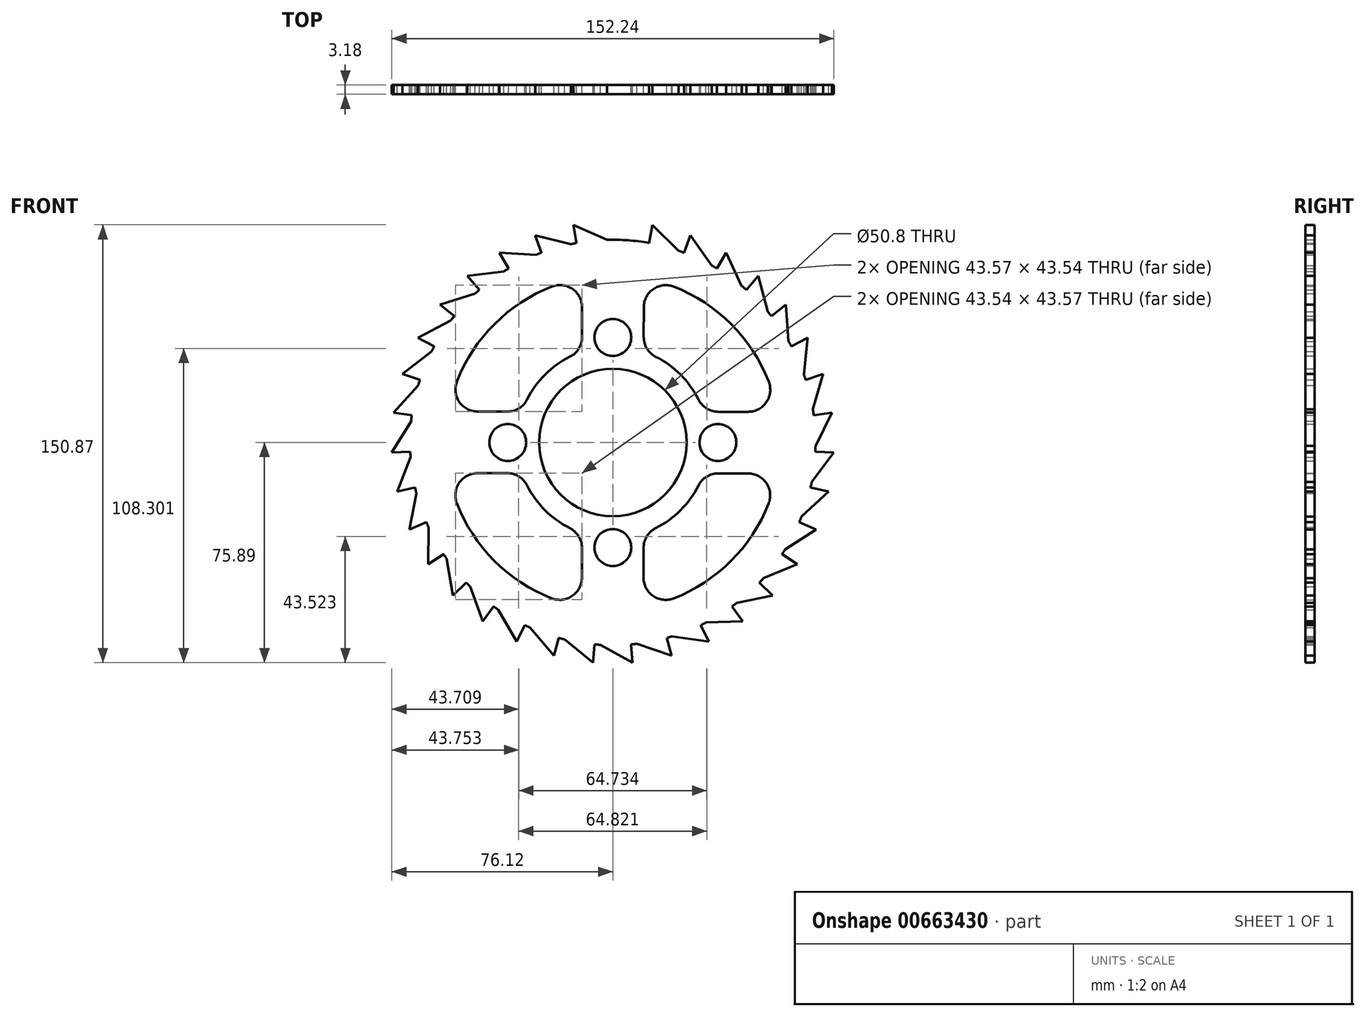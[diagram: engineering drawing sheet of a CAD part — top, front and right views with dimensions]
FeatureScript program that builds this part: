
annotation { "Feature Type Name" : "Feature", "Feature Type Description" : "" }
export const myFeature = defineFeature(function(context is Context, id is Id, definition is map)
    precondition{}
    {
        {
            var Q0;
            Q0=qCreatedBy(makeId("Front.planeOp"),FACE);
            var sketch = newSketch(context, id + "F0", { "sketchPlane" : qUnion([Q0])});
            skCircle(sketch, "E0", {"center": v(0, 0) * mm, "radius": 25.4 * mm});
            skCircle(sketch, "E1", {"center": v(0, 0) * mm, "radius": 69.85 * mm});
            skCircle(sketch, "E2", {"center": v(0, 0) * mm, "radius": 76.2 * mm, "construction": true});
            skLineSegment(sketch, "E3", {"start": v(0, 69.85) * mm, "end": v(0, 76.2) * mm});
            skLineSegment(sketch, "E4", {"start": v(0, 76.2) * mm, "end": v(10.5, 69.06) * mm});
            skLineSegment(sketch, "E5.1.0", {"start": v(13.6, 74.98) * mm, "end": v(22.66, 66.07) * mm});
            skLineSegment(sketch, "E5.1.1", {"start": v(12.47, 68.73) * mm, "end": v(13.6, 74.98) * mm});
            skCircle(sketch, "E5.1.2", {"center": v(0, 0) * mm, "radius": 69.85 * mm, "construction": true});
            skLineSegment(sketch, "E5.2.0", {"start": v(26.77, 71.34) * mm, "end": v(34.1, 60.96) * mm});
            skLineSegment(sketch, "E5.2.1", {"start": v(24.54, 65.4) * mm, "end": v(26.77, 71.34) * mm});
            skCircle(sketch, "E5.2.2", {"center": v(0, 0) * mm, "radius": 69.85 * mm, "construction": true});
            skLineSegment(sketch, "E5.3.0", {"start": v(39.08, 65.41) * mm, "end": v(44.43, 53.9) * mm});
            skLineSegment(sketch, "E5.3.1", {"start": v(35.83, 59.96) * mm, "end": v(39.08, 65.41) * mm});
            skCircle(sketch, "E5.3.2", {"center": v(0, 0) * mm, "radius": 69.85 * mm, "construction": true});
            skLineSegment(sketch, "E5.4.0", {"start": v(50.13, 57.38) * mm, "end": v(53.34, 45.1) * mm});
            skLineSegment(sketch, "E5.4.1", {"start": v(45.96, 52.6) * mm, "end": v(50.13, 57.38) * mm});
            skCircle(sketch, "E5.4.2", {"center": v(0, 0) * mm, "radius": 69.85 * mm, "construction": true});
            skLineSegment(sketch, "E5.5.0", {"start": v(59.58, 47.5) * mm, "end": v(60.54, 34.85) * mm});
            skLineSegment(sketch, "E5.5.1", {"start": v(54.61, 43.55) * mm, "end": v(59.58, 47.5) * mm});
            skCircle(sketch, "E5.5.2", {"center": v(0, 0) * mm, "radius": 69.85 * mm, "construction": true});
            skLineSegment(sketch, "E5.6.0", {"start": v(67.1, 36.1) * mm, "end": v(65.79, 23.48) * mm});
            skLineSegment(sketch, "E5.6.1", {"start": v(61.5, 33.1) * mm, "end": v(67.1, 36.1) * mm});
            skCircle(sketch, "E5.6.2", {"center": v(0, 0) * mm, "radius": 69.85 * mm, "construction": true});
            skLineSegment(sketch, "E5.7.0", {"start": v(72.47, 23.55) * mm, "end": v(68.92, 11.35) * mm});
            skLineSegment(sketch, "E5.7.1", {"start": v(66.43, 21.58) * mm, "end": v(72.47, 23.55) * mm});
            skCircle(sketch, "E5.7.2", {"center": v(0, 0) * mm, "radius": 69.85 * mm, "construction": true});
            skLineSegment(sketch, "E5.8.0", {"start": v(75.51, 10.23) * mm, "end": v(69.84, -1.14) * mm});
            skLineSegment(sketch, "E5.8.1", {"start": v(69.22, 9.38) * mm, "end": v(75.51, 10.23) * mm});
            skCircle(sketch, "E5.8.2", {"center": v(0, 0) * mm, "radius": 69.85 * mm, "construction": true});
            skLineSegment(sketch, "E5.9.0", {"start": v(76.12, -3.42) * mm, "end": v(68.52, -13.59) * mm});
            skLineSegment(sketch, "E5.9.1", {"start": v(69.78, -3.13) * mm, "end": v(76.12, -3.42) * mm});
            skCircle(sketch, "E5.9.2", {"center": v(0, 0) * mm, "radius": 69.85 * mm, "construction": true});
            skLineSegment(sketch, "E5.10.0", {"start": v(74.29, -16.96) * mm, "end": v(64.99, -25.6) * mm});
            skLineSegment(sketch, "E5.10.1", {"start": v(68.1, -15.54) * mm, "end": v(74.29, -16.96) * mm});
            skCircle(sketch, "E5.10.2", {"center": v(0, 0) * mm, "radius": 69.85 * mm, "construction": true});
            skLineSegment(sketch, "E5.11.0", {"start": v(70.07, -29.95) * mm, "end": v(59.37, -36.8) * mm});
            skLineSegment(sketch, "E5.11.1", {"start": v(64.23, -27.45) * mm, "end": v(70.07, -29.95) * mm});
            skCircle(sketch, "E5.11.2", {"center": v(0, 0) * mm, "radius": 69.85 * mm, "construction": true});
            skLineSegment(sketch, "E5.12.0", {"start": v(63.6, -41.98) * mm, "end": v(51.85, -46.8) * mm});
            skLineSegment(sketch, "E5.12.1", {"start": v(58.3, -38.48) * mm, "end": v(63.6, -41.98) * mm});
            skCircle(sketch, "E5.12.2", {"center": v(0, 0) * mm, "radius": 69.85 * mm, "construction": true});
            skLineSegment(sketch, "E5.13.0", {"start": v(55.08, -52.66) * mm, "end": v(42.66, -55.31) * mm});
            skLineSegment(sketch, "E5.13.1", {"start": v(50.49, -48.27) * mm, "end": v(55.08, -52.66) * mm});
            skCircle(sketch, "E5.13.2", {"center": v(0, 0) * mm, "radius": 69.85 * mm, "construction": true});
            skLineSegment(sketch, "E5.14.0", {"start": v(44.79, -61.65) * mm, "end": v(32.1, -62.04) * mm});
            skLineSegment(sketch, "E5.14.1", {"start": v(41.06, -56.5) * mm, "end": v(44.79, -61.65) * mm});
            skCircle(sketch, "E5.14.2", {"center": v(0, 0) * mm, "radius": 69.85 * mm, "construction": true});
            skLineSegment(sketch, "E5.15.0", {"start": v(33.06, -68.65) * mm, "end": v(20.5, -66.77) * mm});
            skLineSegment(sketch, "E5.15.1", {"start": v(30.3, -62.93) * mm, "end": v(33.06, -68.65) * mm});
            skCircle(sketch, "E5.15.2", {"center": v(0, 0) * mm, "radius": 69.85 * mm, "construction": true});
            skLineSegment(sketch, "E5.16.0", {"start": v(20.27, -73.45) * mm, "end": v(8.25, -69.36) * mm});
            skLineSegment(sketch, "E5.16.1", {"start": v(18.58, -67.33) * mm, "end": v(20.27, -73.45) * mm});
            skCircle(sketch, "E5.16.2", {"center": v(0, 0) * mm, "radius": 69.85 * mm, "construction": true});
            skLineSegment(sketch, "E5.17.0", {"start": v(6.83, -75.9) * mm, "end": v(-4.27, -69.72) * mm});
            skLineSegment(sketch, "E5.17.1", {"start": v(6.26, -69.57) * mm, "end": v(6.83, -75.9) * mm});
            skCircle(sketch, "E5.17.2", {"center": v(0, 0) * mm, "radius": 69.85 * mm, "construction": true});
            skLineSegment(sketch, "E5.18.0", {"start": v(-6.83, -75.9) * mm, "end": v(-16.65, -67.84) * mm});
            skLineSegment(sketch, "E5.18.1", {"start": v(-6.26, -69.57) * mm, "end": v(-6.83, -75.9) * mm});
            skCircle(sketch, "E5.18.2", {"center": v(0, 0) * mm, "radius": 69.85 * mm, "construction": true});
            skLineSegment(sketch, "E5.19.0", {"start": v(-20.27, -73.45) * mm, "end": v(-28.5, -63.77) * mm});
            skLineSegment(sketch, "E5.19.1", {"start": v(-18.58, -67.33) * mm, "end": v(-20.27, -73.45) * mm});
            skCircle(sketch, "E5.19.2", {"center": v(0, 0) * mm, "radius": 69.85 * mm, "construction": true});
            skLineSegment(sketch, "E5.20.0", {"start": v(-33.06, -68.65) * mm, "end": v(-39.42, -57.66) * mm});
            skLineSegment(sketch, "E5.20.1", {"start": v(-30.3, -62.93) * mm, "end": v(-33.06, -68.65) * mm});
            skCircle(sketch, "E5.20.2", {"center": v(0, 0) * mm, "radius": 69.85 * mm, "construction": true});
            skLineSegment(sketch, "E5.21.0", {"start": v(-44.79, -61.65) * mm, "end": v(-49.09, -49.7) * mm});
            skLineSegment(sketch, "E5.21.1", {"start": v(-41.06, -56.5) * mm, "end": v(-44.79, -61.65) * mm});
            skCircle(sketch, "E5.21.2", {"center": v(0, 0) * mm, "radius": 69.85 * mm, "construction": true});
            skLineSegment(sketch, "E5.22.0", {"start": v(-55.08, -52.66) * mm, "end": v(-57.17, -40.13) * mm});
            skLineSegment(sketch, "E5.22.1", {"start": v(-50.49, -48.27) * mm, "end": v(-55.08, -52.66) * mm});
            skCircle(sketch, "E5.22.2", {"center": v(0, 0) * mm, "radius": 69.85 * mm, "construction": true});
            skLineSegment(sketch, "E5.23.0", {"start": v(-63.6, -41.98) * mm, "end": v(-63.42, -29.28) * mm});
            skLineSegment(sketch, "E5.23.1", {"start": v(-58.3, -38.48) * mm, "end": v(-63.6, -41.98) * mm});
            skCircle(sketch, "E5.23.2", {"center": v(0, 0) * mm, "radius": 69.85 * mm, "construction": true});
            skLineSegment(sketch, "E5.24.0", {"start": v(-70.07, -29.95) * mm, "end": v(-67.63, -17.49) * mm});
            skLineSegment(sketch, "E5.24.1", {"start": v(-64.23, -27.45) * mm, "end": v(-70.07, -29.95) * mm});
            skCircle(sketch, "E5.24.2", {"center": v(0, 0) * mm, "radius": 69.85 * mm, "construction": true});
            skLineSegment(sketch, "E5.25.0", {"start": v(-74.29, -16.96) * mm, "end": v(-69.66, -5.13) * mm});
            skLineSegment(sketch, "E5.25.1", {"start": v(-68.1, -15.54) * mm, "end": v(-74.29, -16.96) * mm});
            skCircle(sketch, "E5.25.2", {"center": v(0, 0) * mm, "radius": 69.85 * mm, "construction": true});
            skLineSegment(sketch, "E5.26.0", {"start": v(-76.12, -3.42) * mm, "end": v(-69.46, 7.4) * mm});
            skLineSegment(sketch, "E5.26.1", {"start": v(-69.78, -3.13) * mm, "end": v(-76.12, -3.42) * mm});
            skCircle(sketch, "E5.26.2", {"center": v(0, 0) * mm, "radius": 69.85 * mm, "construction": true});
            skLineSegment(sketch, "E5.27.0", {"start": v(-75.51, 10.23) * mm, "end": v(-67.02, 19.67) * mm});
            skLineSegment(sketch, "E5.27.1", {"start": v(-69.22, 9.38) * mm, "end": v(-75.51, 10.23) * mm});
            skCircle(sketch, "E5.27.2", {"center": v(0, 0) * mm, "radius": 69.85 * mm, "construction": true});
            skLineSegment(sketch, "E5.28.0", {"start": v(-72.47, 23.55) * mm, "end": v(-62.43, 31.33) * mm});
            skLineSegment(sketch, "E5.28.1", {"start": v(-66.43, 21.58) * mm, "end": v(-72.47, 23.55) * mm});
            skCircle(sketch, "E5.28.2", {"center": v(0, 0) * mm, "radius": 69.85 * mm, "construction": true});
            skLineSegment(sketch, "E5.29.0", {"start": v(-67.1, 36.1) * mm, "end": v(-55.83, 41.97) * mm});
            skLineSegment(sketch, "E5.29.1", {"start": v(-61.5, 33.1) * mm, "end": v(-67.1, 36.1) * mm});
            skCircle(sketch, "E5.29.2", {"center": v(0, 0) * mm, "radius": 69.85 * mm, "construction": true});
            skLineSegment(sketch, "E5.30.0", {"start": v(-59.58, 47.5) * mm, "end": v(-47.44, 51.27) * mm});
            skLineSegment(sketch, "E5.30.1", {"start": v(-54.61, 43.55) * mm, "end": v(-59.58, 47.5) * mm});
            skCircle(sketch, "E5.30.2", {"center": v(0, 0) * mm, "radius": 69.85 * mm, "construction": true});
            skLineSegment(sketch, "E5.31.0", {"start": v(-50.13, 57.38) * mm, "end": v(-37.53, 58.91) * mm});
            skLineSegment(sketch, "E5.31.1", {"start": v(-45.96, 52.6) * mm, "end": v(-50.13, 57.38) * mm});
            skCircle(sketch, "E5.31.2", {"center": v(0, 0) * mm, "radius": 69.85 * mm, "construction": true});
            skLineSegment(sketch, "E5.32.0", {"start": v(-39.08, 65.41) * mm, "end": v(-26.4, 64.67) * mm});
            skLineSegment(sketch, "E5.32.1", {"start": v(-35.83, 59.96) * mm, "end": v(-39.08, 65.41) * mm});
            skCircle(sketch, "E5.32.2", {"center": v(0, 0) * mm, "radius": 69.85 * mm, "construction": true});
            skLineSegment(sketch, "E5.33.0", {"start": v(-26.77, 71.34) * mm, "end": v(-14.43, 68.34) * mm});
            skLineSegment(sketch, "E5.33.1", {"start": v(-24.54, 65.4) * mm, "end": v(-26.77, 71.34) * mm});
            skCircle(sketch, "E5.33.2", {"center": v(0, 0) * mm, "radius": 69.85 * mm, "construction": true});
            skLineSegment(sketch, "E5.34.0", {"start": v(-13.6, 74.98) * mm, "end": v(-2, 69.82) * mm});
            skLineSegment(sketch, "E5.34.1", {"start": v(-12.47, 68.73) * mm, "end": v(-13.6, 74.98) * mm});
            skCircle(sketch, "E5.34.2", {"center": v(0, 0) * mm, "radius": 69.85 * mm, "construction": true});
            skCircle(sketch, "E5.35.2", {"center": v(0, 0) * mm, "radius": 69.85 * mm, "construction": true});
            skLineSegment(sketch, "E5.anchor1", {"start": v(0, 0) * mm, "end": v(0, 76.2) * mm, "construction": true});
            skLineSegment(sketch, "E5.anchor2", {"start": v(0, 0) * mm, "end": v(0, 76.2) * mm, "construction": true});
            skCircle(sketch, "E6", {"center": v(0, 36.19) * mm, "radius": 6.35 * mm});
            skCircle(sketch, "E7.1.0", {"center": v(-36.19, 0) * mm, "radius": 6.35 * mm});
            skCircle(sketch, "E7.2.0", {"center": v(0, -36.19) * mm, "radius": 6.35 * mm});
            skCircle(sketch, "E7.3.0", {"center": v(36.19, 0) * mm, "radius": 6.35 * mm});
            skArc(sketch, "E8", {"start": v(-14.79, 29.52) * mm, "mid": v(-23.33, 23.37) * mm, "end": v(-29.5, 14.84) * mm});
            skLineSegment(sketch, "E9", {"start": v(-10.58, 36.34) * mm, "end": v(-10.58, 46.61) * mm});
            skArc(sketch, "E10", {"start": v(-20.97, 53.7) * mm, "mid": v(-40.74, 40.8) * mm, "end": v(-53.67, 21.06) * mm});
            skLineSegment(sketch, "E11", {"start": v(-46.6, 10.66) * mm, "end": v(-36.32, 10.64) * mm});
            skPoint(sketch, "E12.visualSharp", {"position": v(-31.26, 10.63) * mm});
            skArc(sketch, "E12.filletArc", {"start": v(-36.32, 10.64) * mm, "mid": v(-32.31, 11.77) * mm, "end": v(-29.5, 14.84) * mm});
            skPoint(sketch, "E13.visualSharp", {"position": v(-56.66, 10.67) * mm});
            skArc(sketch, "E13.filletArc", {"start": v(-53.67, 21.06) * mm, "mid": v(-52.88, 13.99) * mm, "end": v(-46.6, 10.66) * mm});
            skPoint(sketch, "E14.visualSharp", {"position": v(-10.58, 56.68) * mm});
            skArc(sketch, "E14.filletArc", {"start": v(-10.58, 46.61) * mm, "mid": v(-13.9, 52.9) * mm, "end": v(-20.97, 53.7) * mm});
            skPoint(sketch, "E15.visualSharp", {"position": v(-10.58, 31.28) * mm});
            skArc(sketch, "E15.filletArc", {"start": v(-14.79, 29.52) * mm, "mid": v(-11.72, 32.33) * mm, "end": v(-10.58, 36.34) * mm});
            skArc(sketch, "E16.1.0", {"start": v(-29.52, -14.79) * mm, "mid": v(-23.37, -23.33) * mm, "end": v(-14.84, -29.5) * mm});
            skLineSegment(sketch, "E16.1.1", {"start": v(-36.34, -10.58) * mm, "end": v(-46.61, -10.58) * mm});
            skArc(sketch, "E16.1.2", {"start": v(-29.52, -14.79) * mm, "mid": v(-32.33, -11.72) * mm, "end": v(-36.34, -10.58) * mm});
            skArc(sketch, "E16.1.3", {"start": v(-46.61, -10.58) * mm, "mid": v(-52.9, -13.9) * mm, "end": v(-53.7, -20.97) * mm});
            skArc(sketch, "E16.1.4", {"start": v(-53.7, -20.97) * mm, "mid": v(-40.8, -40.74) * mm, "end": v(-21.06, -53.67) * mm});
            skArc(sketch, "E16.1.5", {"start": v(-21.06, -53.67) * mm, "mid": v(-13.99, -52.88) * mm, "end": v(-10.66, -46.6) * mm});
            skLineSegment(sketch, "E16.1.6", {"start": v(-10.66, -46.6) * mm, "end": v(-10.64, -36.32) * mm});
            skArc(sketch, "E16.1.7", {"start": v(-10.64, -36.32) * mm, "mid": v(-11.77, -32.31) * mm, "end": v(-14.84, -29.5) * mm});
            skArc(sketch, "E16.2.0", {"start": v(14.79, -29.52) * mm, "mid": v(23.33, -23.37) * mm, "end": v(29.5, -14.84) * mm});
            skLineSegment(sketch, "E16.2.1", {"start": v(10.58, -36.34) * mm, "end": v(10.58, -46.61) * mm});
            skArc(sketch, "E16.2.2", {"start": v(14.79, -29.52) * mm, "mid": v(11.72, -32.33) * mm, "end": v(10.58, -36.34) * mm});
            skArc(sketch, "E16.2.3", {"start": v(10.58, -46.61) * mm, "mid": v(13.9, -52.9) * mm, "end": v(20.97, -53.7) * mm});
            skArc(sketch, "E16.2.4", {"start": v(20.97, -53.7) * mm, "mid": v(40.74, -40.8) * mm, "end": v(53.67, -21.06) * mm});
            skArc(sketch, "E16.2.5", {"start": v(53.67, -21.06) * mm, "mid": v(52.88, -13.99) * mm, "end": v(46.6, -10.66) * mm});
            skLineSegment(sketch, "E16.2.6", {"start": v(46.6, -10.66) * mm, "end": v(36.32, -10.64) * mm});
            skArc(sketch, "E16.2.7", {"start": v(36.32, -10.64) * mm, "mid": v(32.31, -11.77) * mm, "end": v(29.5, -14.84) * mm});
            skArc(sketch, "E16.3.0", {"start": v(29.52, 14.79) * mm, "mid": v(23.37, 23.33) * mm, "end": v(14.84, 29.5) * mm});
            skLineSegment(sketch, "E16.3.1", {"start": v(36.34, 10.58) * mm, "end": v(46.61, 10.58) * mm});
            skArc(sketch, "E16.3.2", {"start": v(29.52, 14.79) * mm, "mid": v(32.33, 11.72) * mm, "end": v(36.34, 10.58) * mm});
            skArc(sketch, "E16.3.3", {"start": v(46.61, 10.58) * mm, "mid": v(52.9, 13.9) * mm, "end": v(53.7, 20.97) * mm});
            skArc(sketch, "E16.3.4", {"start": v(53.7, 20.97) * mm, "mid": v(40.8, 40.74) * mm, "end": v(21.06, 53.67) * mm});
            skArc(sketch, "E16.3.5", {"start": v(21.06, 53.67) * mm, "mid": v(13.99, 52.88) * mm, "end": v(10.66, 46.6) * mm});
            skLineSegment(sketch, "E16.3.6", {"start": v(10.66, 46.6) * mm, "end": v(10.64, 36.32) * mm});
            skArc(sketch, "E16.3.7", {"start": v(10.64, 36.32) * mm, "mid": v(11.77, 32.31) * mm, "end": v(14.84, 29.5) * mm});
            skSolve(sketch);
        }
        {
            var Q0;
            Q0=makeQuery(id+"F0.imprint","IMPRINT",FACE,{"disambiguationData":[TD([[makeQuery(id+"F0.imprint","IMPRINT",EDGE,{"derivedFrom":sQuery(id+"F0.wireOp",EDGE,"E0")}),-1.0]])]});
            var Q1;
            {var subQ0=sQuery(id+"F0.wireOp",EDGE,"E5.8.0");Q1=makeQuery(id+"F0.imprint","IMPRINT",FACE,{"disambiguationData":[TD([[makeQuery(id+"F0.imprint","IMPRINT",EDGE,{"derivedFrom":subQ0}),-1.0]])]});}
            var Q2;
            {var subQ0=sQuery(id+"F0.wireOp",EDGE,"E5.7.0");Q2=makeQuery(id+"F0.imprint","IMPRINT",FACE,{"disambiguationData":[TD([[makeQuery(id+"F0.imprint","IMPRINT",EDGE,{"derivedFrom":subQ0}),-1.0]])]});}
            var Q3;
            {var subQ0=sQuery(id+"F0.wireOp",EDGE,"E5.6.0");Q3=makeQuery(id+"F0.imprint","IMPRINT",FACE,{"disambiguationData":[TD([[makeQuery(id+"F0.imprint","IMPRINT",EDGE,{"derivedFrom":subQ0}),-1.0]])]});}
            var Q4;
            {var subQ0=sQuery(id+"F0.wireOp",EDGE,"E5.5.0");Q4=makeQuery(id+"F0.imprint","IMPRINT",FACE,{"disambiguationData":[TD([[makeQuery(id+"F0.imprint","IMPRINT",EDGE,{"derivedFrom":subQ0}),-1.0]])]});}
            var Q5;
            {var subQ0=sQuery(id+"F0.wireOp",EDGE,"E5.4.0");Q5=makeQuery(id+"F0.imprint","IMPRINT",FACE,{"disambiguationData":[TD([[makeQuery(id+"F0.imprint","IMPRINT",EDGE,{"derivedFrom":subQ0}),-1.0]])]});}
            var Q6;
            {var subQ0=sQuery(id+"F0.wireOp",EDGE,"E5.3.0");Q6=makeQuery(id+"F0.imprint","IMPRINT",FACE,{"disambiguationData":[TD([[makeQuery(id+"F0.imprint","IMPRINT",EDGE,{"derivedFrom":subQ0}),-1.0]])]});}
            var Q7;
            {var subQ0=sQuery(id+"F0.wireOp",EDGE,"E5.2.0");Q7=makeQuery(id+"F0.imprint","IMPRINT",FACE,{"disambiguationData":[TD([[makeQuery(id+"F0.imprint","IMPRINT",EDGE,{"derivedFrom":subQ0}),-1.0]])]});}
            var Q8;
            {var subQ0=sQuery(id+"F0.wireOp",EDGE,"E5.1.0");Q8=makeQuery(id+"F0.imprint","IMPRINT",FACE,{"disambiguationData":[TD([[makeQuery(id+"F0.imprint","IMPRINT",EDGE,{"derivedFrom":subQ0}),-1.0]])]});}
            var Q9;
            {var subQ0=sQuery(id+"F0.wireOp",EDGE,"E4");Q9=makeQuery(id+"F0.imprint","IMPRINT",FACE,{"disambiguationData":[TD([[makeQuery(id+"F0.imprint","IMPRINT",EDGE,{"derivedFrom":subQ0}),-1.0]])]});}
            var Q10;
            {var subQ0=sQuery(id+"F0.wireOp",EDGE,"E5.34.0");Q10=makeQuery(id+"F0.imprint","IMPRINT",FACE,{"disambiguationData":[TD([[makeQuery(id+"F0.imprint","IMPRINT",EDGE,{"derivedFrom":subQ0}),-1.0]])]});}
            var Q11;
            {var subQ0=sQuery(id+"F0.wireOp",EDGE,"E5.33.0");Q11=makeQuery(id+"F0.imprint","IMPRINT",FACE,{"disambiguationData":[TD([[makeQuery(id+"F0.imprint","IMPRINT",EDGE,{"derivedFrom":subQ0}),-1.0]])]});}
            var Q12;
            {var subQ0=sQuery(id+"F0.wireOp",EDGE,"E5.32.0");Q12=makeQuery(id+"F0.imprint","IMPRINT",FACE,{"disambiguationData":[TD([[makeQuery(id+"F0.imprint","IMPRINT",EDGE,{"derivedFrom":subQ0}),-1.0]])]});}
            var Q13;
            {var subQ0=sQuery(id+"F0.wireOp",EDGE,"E5.31.0");Q13=makeQuery(id+"F0.imprint","IMPRINT",FACE,{"disambiguationData":[TD([[makeQuery(id+"F0.imprint","IMPRINT",EDGE,{"derivedFrom":subQ0}),-1.0]])]});}
            var Q14;
            {var subQ0=sQuery(id+"F0.wireOp",EDGE,"E5.30.0");Q14=makeQuery(id+"F0.imprint","IMPRINT",FACE,{"disambiguationData":[TD([[makeQuery(id+"F0.imprint","IMPRINT",EDGE,{"derivedFrom":subQ0}),-1.0]])]});}
            var Q15;
            {var subQ0=sQuery(id+"F0.wireOp",EDGE,"E5.29.0");Q15=makeQuery(id+"F0.imprint","IMPRINT",FACE,{"disambiguationData":[TD([[makeQuery(id+"F0.imprint","IMPRINT",EDGE,{"derivedFrom":subQ0}),-1.0]])]});}
            var Q16;
            {var subQ0=sQuery(id+"F0.wireOp",EDGE,"E5.28.0");Q16=makeQuery(id+"F0.imprint","IMPRINT",FACE,{"disambiguationData":[TD([[makeQuery(id+"F0.imprint","IMPRINT",EDGE,{"derivedFrom":subQ0}),-1.0]])]});}
            var Q17;
            {var subQ0=sQuery(id+"F0.wireOp",EDGE,"E5.27.0");Q17=makeQuery(id+"F0.imprint","IMPRINT",FACE,{"disambiguationData":[TD([[makeQuery(id+"F0.imprint","IMPRINT",EDGE,{"derivedFrom":subQ0}),-1.0]])]});}
            var Q18;
            {var subQ0=sQuery(id+"F0.wireOp",EDGE,"E5.26.0");Q18=makeQuery(id+"F0.imprint","IMPRINT",FACE,{"disambiguationData":[TD([[makeQuery(id+"F0.imprint","IMPRINT",EDGE,{"derivedFrom":subQ0}),-1.0]])]});}
            var Q19;
            {var subQ0=sQuery(id+"F0.wireOp",EDGE,"E5.25.0");Q19=makeQuery(id+"F0.imprint","IMPRINT",FACE,{"disambiguationData":[TD([[makeQuery(id+"F0.imprint","IMPRINT",EDGE,{"derivedFrom":subQ0}),-1.0]])]});}
            var Q20;
            {var subQ0=sQuery(id+"F0.wireOp",EDGE,"E5.24.0");Q20=makeQuery(id+"F0.imprint","IMPRINT",FACE,{"disambiguationData":[TD([[makeQuery(id+"F0.imprint","IMPRINT",EDGE,{"derivedFrom":subQ0}),-1.0]])]});}
            var Q21;
            {var subQ0=sQuery(id+"F0.wireOp",EDGE,"E5.23.0");Q21=makeQuery(id+"F0.imprint","IMPRINT",FACE,{"disambiguationData":[TD([[makeQuery(id+"F0.imprint","IMPRINT",EDGE,{"derivedFrom":subQ0}),-1.0]])]});}
            var Q22;
            {var subQ0=sQuery(id+"F0.wireOp",EDGE,"E5.22.0");Q22=makeQuery(id+"F0.imprint","IMPRINT",FACE,{"disambiguationData":[TD([[makeQuery(id+"F0.imprint","IMPRINT",EDGE,{"derivedFrom":subQ0}),-1.0]])]});}
            var Q23;
            {var subQ0=sQuery(id+"F0.wireOp",EDGE,"E5.21.0");Q23=makeQuery(id+"F0.imprint","IMPRINT",FACE,{"disambiguationData":[TD([[makeQuery(id+"F0.imprint","IMPRINT",EDGE,{"derivedFrom":subQ0}),-1.0]])]});}
            var Q24;
            {var subQ0=sQuery(id+"F0.wireOp",EDGE,"E5.20.0");Q24=makeQuery(id+"F0.imprint","IMPRINT",FACE,{"disambiguationData":[TD([[makeQuery(id+"F0.imprint","IMPRINT",EDGE,{"derivedFrom":subQ0}),-1.0]])]});}
            var Q25;
            {var subQ0=sQuery(id+"F0.wireOp",EDGE,"E5.19.0");Q25=makeQuery(id+"F0.imprint","IMPRINT",FACE,{"disambiguationData":[TD([[makeQuery(id+"F0.imprint","IMPRINT",EDGE,{"derivedFrom":subQ0}),-1.0]])]});}
            var Q26;
            {var subQ0=sQuery(id+"F0.wireOp",EDGE,"E5.18.0");Q26=makeQuery(id+"F0.imprint","IMPRINT",FACE,{"disambiguationData":[TD([[makeQuery(id+"F0.imprint","IMPRINT",EDGE,{"derivedFrom":subQ0}),-1.0]])]});}
            var Q27;
            {var subQ0=sQuery(id+"F0.wireOp",EDGE,"E5.17.0");Q27=makeQuery(id+"F0.imprint","IMPRINT",FACE,{"disambiguationData":[TD([[makeQuery(id+"F0.imprint","IMPRINT",EDGE,{"derivedFrom":subQ0}),-1.0]])]});}
            var Q28;
            {var subQ0=sQuery(id+"F0.wireOp",EDGE,"E5.16.0");Q28=makeQuery(id+"F0.imprint","IMPRINT",FACE,{"disambiguationData":[TD([[makeQuery(id+"F0.imprint","IMPRINT",EDGE,{"derivedFrom":subQ0}),-1.0]])]});}
            var Q29;
            {var subQ0=sQuery(id+"F0.wireOp",EDGE,"E5.15.0");Q29=makeQuery(id+"F0.imprint","IMPRINT",FACE,{"disambiguationData":[TD([[makeQuery(id+"F0.imprint","IMPRINT",EDGE,{"derivedFrom":subQ0}),-1.0]])]});}
            var Q30;
            {var subQ0=sQuery(id+"F0.wireOp",EDGE,"E5.14.0");Q30=makeQuery(id+"F0.imprint","IMPRINT",FACE,{"disambiguationData":[TD([[makeQuery(id+"F0.imprint","IMPRINT",EDGE,{"derivedFrom":subQ0}),-1.0]])]});}
            var Q31;
            {var subQ0=sQuery(id+"F0.wireOp",EDGE,"E5.13.0");Q31=makeQuery(id+"F0.imprint","IMPRINT",FACE,{"disambiguationData":[TD([[makeQuery(id+"F0.imprint","IMPRINT",EDGE,{"derivedFrom":subQ0}),-1.0]])]});}
            var Q32;
            {var subQ0=sQuery(id+"F0.wireOp",EDGE,"E5.12.0");Q32=makeQuery(id+"F0.imprint","IMPRINT",FACE,{"disambiguationData":[TD([[makeQuery(id+"F0.imprint","IMPRINT",EDGE,{"derivedFrom":subQ0}),-1.0]])]});}
            var Q33;
            {var subQ0=sQuery(id+"F0.wireOp",EDGE,"E5.11.0");Q33=makeQuery(id+"F0.imprint","IMPRINT",FACE,{"disambiguationData":[TD([[makeQuery(id+"F0.imprint","IMPRINT",EDGE,{"derivedFrom":subQ0}),-1.0]])]});}
            var Q34;
            {var subQ0=sQuery(id+"F0.wireOp",EDGE,"E5.10.0");Q34=makeQuery(id+"F0.imprint","IMPRINT",FACE,{"disambiguationData":[TD([[makeQuery(id+"F0.imprint","IMPRINT",EDGE,{"derivedFrom":subQ0}),-1.0]])]});}
            var Q35;
            {var subQ0=sQuery(id+"F0.wireOp",EDGE,"E5.9.0");Q35=makeQuery(id+"F0.imprint","IMPRINT",FACE,{"disambiguationData":[TD([[makeQuery(id+"F0.imprint","IMPRINT",EDGE,{"derivedFrom":subQ0}),-1.0]])]});}
            extrude(context, id + "F1", {"entities" : qUnion([Q0, Q1, Q2, Q3, Q4, Q5, Q6, Q7, Q8, Q9, Q10, Q11, Q12, Q13, Q14, Q15, Q16, Q17, Q18, Q19, Q20, Q21, Q22, Q23, Q24, Q25, Q26, Q27, Q28, Q29, Q30, Q31, Q32, Q33, Q34, Q35]), "depth" : 3.17 * mm, "offsetDistance" : 25.4 * mm});
        }
    });
